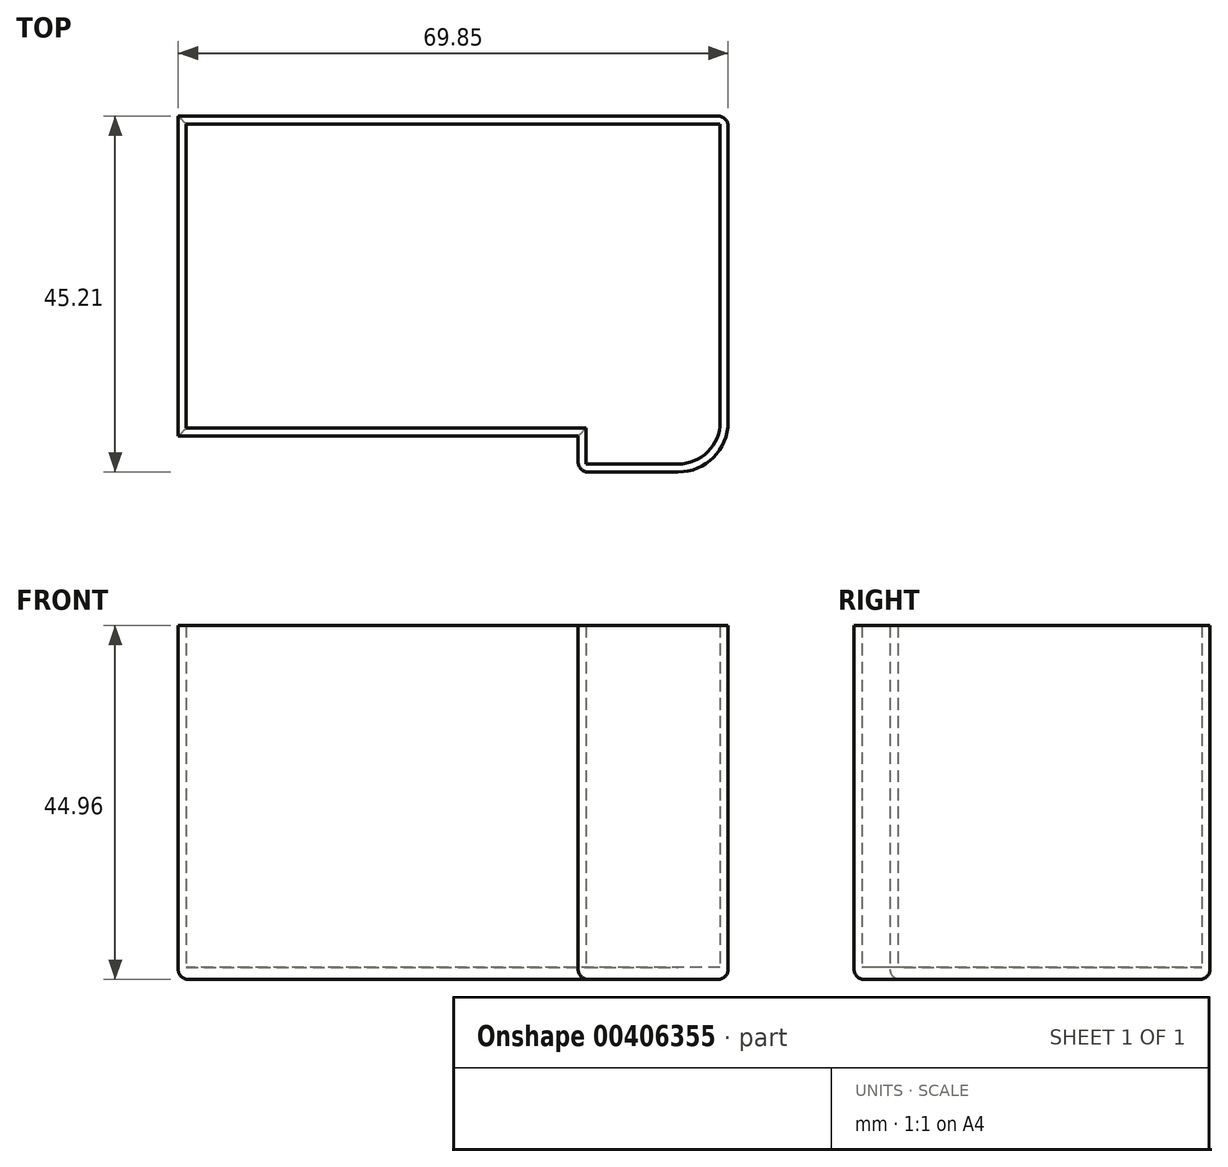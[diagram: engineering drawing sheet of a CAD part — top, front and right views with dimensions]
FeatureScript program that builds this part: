
annotation { "Feature Type Name" : "Feature", "Feature Type Description" : "" }
export const myFeature = defineFeature(function(context is Context, id is Id, definition is map)
    precondition{}
    {
        {
            var Q0;
            Q0=qCreatedBy(makeId("Top.planeOp"),FACE);
            var sketch = newSketch(context, id + "F0", { "sketchPlane" : qUnion([Q0])});
            skLineSegment(sketch, "E0", {"start": v(-35.58, -17.32) * mm, "end": v(-35.58, 21.54) * mm});
            skLineSegment(sketch, "E1", {"start": v(-35.58, 21.54) * mm, "end": v(34.27, 21.54) * mm});
            skLineSegment(sketch, "E2", {"start": v(34.27, 21.54) * mm, "end": v(34.27, -19.1) * mm});
            skLineSegment(sketch, "E3", {"start": v(34.27, -19.1) * mm, "end": v(-16.53, -19.1) * mm});
            skLineSegment(sketch, "E4", {"start": v(-16.53, -19.1) * mm, "end": v(-16.53, -23.67) * mm});
            skLineSegment(sketch, "E5", {"start": v(-16.53, -23.67) * mm, "end": v(-29.23, -23.67) * mm});
            skPoint(sketch, "E6.visualSharp", {"position": v(-35.58, -23.67) * mm});
            skArc(sketch, "E6.filletArc", {"start": v(-35.58, -17.32) * mm, "mid": v(-33.72, -21.81) * mm, "end": v(-29.23, -23.67) * mm});
            skSolve(sketch);
        }
        {
            var Q0;
            Q0=makeQuery(id+"F0.imprint","IMPRINT",FACE,{"disambiguationData":[TD([[makeQuery(id+"F0.imprint","IMPRINT",EDGE,{"derivedFrom":sQuery(id+"F0.wireOp",EDGE,"E0")}),-1.0]])]});
            extrude(context, id + "F1", {"entities" : qUnion([Q0]), "depth" : 1.52 * mm});
        }
        {
            var Q0;
            Q0=makeQuery(id+"F1.opExtrude","CAP_FACE",FACE,{"disambiguationData":[OSD([sQuery(id+"F0.wireOp",EDGE,"E0"),sQuery(id+"F0.wireOp",EDGE,"E1"),sQuery(id+"F0.wireOp",EDGE,"E2"),sQuery(id+"F0.wireOp",EDGE,"E3"),sQuery(id+"F0.wireOp",EDGE,"E4"),sQuery(id+"F0.wireOp",EDGE,"E5"),sQuery(id+"F0.wireOp",EDGE,"E6.filletArc")])],"isStart":false});
            var sketch = newSketch(context, id + "F2", { "sketchPlane" : qUnion([Q0])});
            skLineSegment(sketch, "E7", {"start": v(-35.58, -17.32) * mm, "end": v(-35.58, 21.54) * mm});
            skLineSegment(sketch, "E8", {"start": v(-35.58, 21.54) * mm, "end": v(34.27, 21.54) * mm});
            skLineSegment(sketch, "E9", {"start": v(34.27, 21.54) * mm, "end": v(34.27, -19.1) * mm});
            skLineSegment(sketch, "E10", {"start": v(34.27, -19.1) * mm, "end": v(-16.53, -19.1) * mm});
            skLineSegment(sketch, "E11", {"start": v(-16.53, -19.1) * mm, "end": v(-16.53, -23.67) * mm});
            skLineSegment(sketch, "E12", {"start": v(-16.53, -23.67) * mm, "end": v(-29.23, -23.67) * mm});
            skPoint(sketch, "E13.visualSharp", {"position": v(-35.58, -23.67) * mm});
            skArc(sketch, "E13.filletArc", {"start": v(-35.58, -17.32) * mm, "mid": v(-33.72, -21.81) * mm, "end": v(-29.23, -23.67) * mm});
            skLineSegment(sketch, "E14.0", {"start": v(-17.55, -18.09) * mm, "end": v(-17.55, -22.66) * mm});
            skLineSegment(sketch, "E14.1", {"start": v(-34.56, -17.32) * mm, "end": v(-34.56, 20.52) * mm});
            skLineSegment(sketch, "E14.2", {"start": v(-34.56, 20.52) * mm, "end": v(33.25, 20.52) * mm});
            skLineSegment(sketch, "E14.3", {"start": v(-17.55, -22.66) * mm, "end": v(-29.23, -22.66) * mm});
            skLineSegment(sketch, "E14.4", {"start": v(33.25, 20.52) * mm, "end": v(33.25, -18.09) * mm});
            skLineSegment(sketch, "E14.5", {"start": v(33.25, -18.09) * mm, "end": v(-17.55, -18.09) * mm});
            skPoint(sketch, "E15.visualSharp", {"position": v(-34.56, -22.66) * mm});
            skArc(sketch, "E15.filletArc", {"start": v(-34.56, -17.32) * mm, "mid": v(-33, -21.1) * mm, "end": v(-29.23, -22.66) * mm});
            skSolve(sketch);
        }
        {
            var Q0;
            Q0=qSketchRegion(id+"F2",true);
            extrude(context, id + "F3", {"entities" : qUnion([Q0]), "operationType" : NewBodyOperationType.ADD, "depth" : 43.43 * mm});
        }
        {
            var Q0;
            Q0=makeQuery(id+"F1.opExtrude","CAP_FACE",FACE,{"disambiguationData":[OSD([sQuery(id+"F0.wireOp",EDGE,"E0"),sQuery(id+"F0.wireOp",EDGE,"E1"),sQuery(id+"F0.wireOp",EDGE,"E2"),sQuery(id+"F0.wireOp",EDGE,"E3"),sQuery(id+"F0.wireOp",EDGE,"E4"),sQuery(id+"F0.wireOp",EDGE,"E5"),sQuery(id+"F0.wireOp",EDGE,"E6.filletArc")])],"isStart":true});
            fillet(context, id + "F4", {"entities" : qUnion([Q0]), "radius" : 1.27 * mm, "tangentPropagation" : true, "allowEdgeOverflow" : false});
        }
        {
            var Q0;
            Q0=makeQuery(id+"F3.boolean.opBoolean","MERGE",EDGE,{"derivedFrom":[makeQuery(id+"F1.opExtrude","SWEPT_EDGE",EDGE,{"disambiguationData":[OSD([sQuery(id+"F0.wireOp",EDGE,"E4"),sQuery(id+"F0.wireOp",EDGE,"E5")])]}),makeQuery(id+"F3.opExtrude","SWEPT_EDGE",EDGE,{"disambiguationData":[OSD([sQuery(id+"F2.wireOp",EDGE,"E11"),sQuery(id+"F2.wireOp",EDGE,"E12")])]})]});
            var Q1;
            Q1=makeQuery(id+"F3.boolean.opBoolean","MERGE",EDGE,{"derivedFrom":[makeQuery(id+"F1.opExtrude","SWEPT_EDGE",EDGE,{"disambiguationData":[OSD([sQuery(id+"F0.wireOp",EDGE,"E0"),sQuery(id+"F0.wireOp",EDGE,"E1")])]}),makeQuery(id+"F3.opExtrude","SWEPT_EDGE",EDGE,{"disambiguationData":[OSD([sQuery(id+"F2.wireOp",EDGE,"E7"),sQuery(id+"F2.wireOp",EDGE,"E8")])]})]});
            fillet(context, id + "F5", {"entities" : qUnion([Q0, Q1]), "radius" : 1.27 * mm, "tangentPropagation" : true, "allowEdgeOverflow" : false});
        }
        {
            var Q0;
            Q0=makeQuery(id+"F1.opExtrude","SWEPT_BODY",BODY,{"disambiguationData":[OSD([sQuery(id+"F0.wireOp",EDGE,"E0"),sQuery(id+"F0.wireOp",EDGE,"E1"),sQuery(id+"F0.wireOp",EDGE,"E2"),sQuery(id+"F0.wireOp",EDGE,"E3"),sQuery(id+"F0.wireOp",EDGE,"E4"),sQuery(id+"F0.wireOp",EDGE,"E5"),sQuery(id+"F0.wireOp",EDGE,"E6.filletArc")])]});
            var Q1;
            Q1=makeQuery(id+"F3.boolean.opBoolean","MERGE",FACE,{"derivedFrom":[makeQuery(id+"F1.opExtrude","SWEPT_FACE",FACE,{"disambiguationData":[OSD([sQuery(id+"F0.wireOp",EDGE,"E2")])]}),makeQuery(id+"F3.opExtrude","SWEPT_FACE",FACE,{"disambiguationData":[OSD([sQuery(id+"F2.wireOp",EDGE,"E9")])]})]});
            mirror(context, id + "F6", {"entities" : qUnion([Q0]), "mirrorPlane" : qUnion([Q1])});
        }
        {
            var Q0;
            Q0=makeQuery(id+"F1.opExtrude","SWEPT_BODY",BODY,{"disambiguationData":[OSD([sQuery(id+"F0.wireOp",EDGE,"E0"),sQuery(id+"F0.wireOp",EDGE,"E1"),sQuery(id+"F0.wireOp",EDGE,"E2"),sQuery(id+"F0.wireOp",EDGE,"E3"),sQuery(id+"F0.wireOp",EDGE,"E4"),sQuery(id+"F0.wireOp",EDGE,"E5"),sQuery(id+"F0.wireOp",EDGE,"E6.filletArc")])]});
            deleteBodies(context, id + "F7", {"entities" : qUnion([Q0])});
        }
    });
